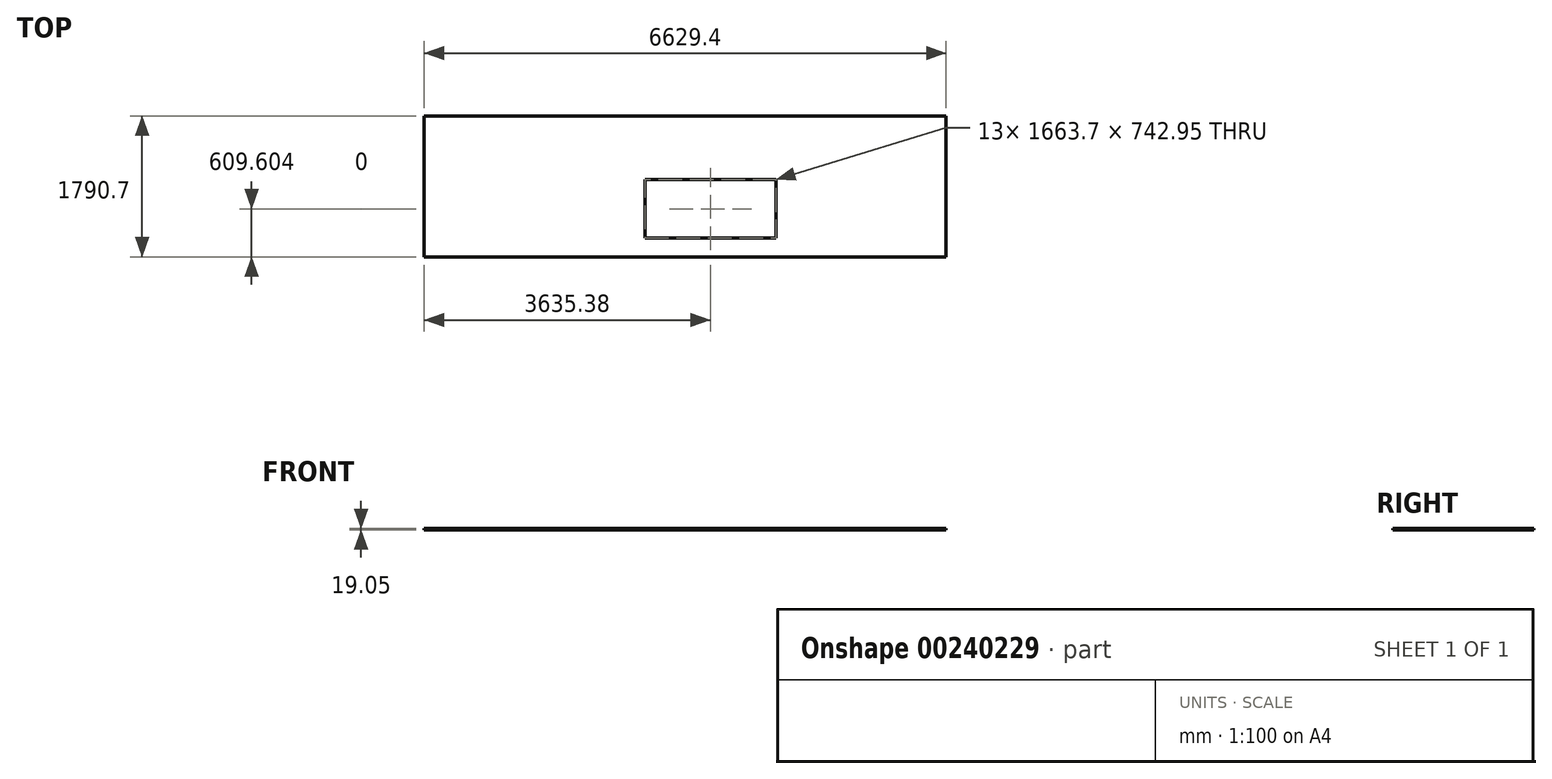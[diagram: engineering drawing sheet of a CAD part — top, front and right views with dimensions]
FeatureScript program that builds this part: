
annotation { "Feature Type Name" : "Feature", "Feature Type Description" : "" }
export const myFeature = defineFeature(function(context is Context, id is Id, definition is map)
    precondition{}
    {
        {
            var Q0;
            Q0=qCreatedBy(makeId("Top.planeOp"),FACE);
            var sketch = newSketch(context, id + "F0", { "sketchPlane" : qUnion([Q0])});
            skLineSegment(sketch, "E0.top", {"start": v(3079.82, 1055.16) * mm, "end": v(-3549.58, 1055.16) * mm});
            skLineSegment(sketch, "E0.left", {"start": v(3079.82, 1055.16) * mm, "end": v(3079.82, 1055.16) * mm});
            skLineSegment(sketch, "E1.top", {"start": v(-3549.58, -735.54) * mm, "end": v(3079.82, -735.54) * mm});
            skLineSegment(sketch, "E2.bottom", {"start": v(-3549.58, 1055.16) * mm, "end": v(3079.82, 1055.16) * mm});
            skLineSegment(sketch, "E2.left", {"start": v(-3549.58, 1055.16) * mm, "end": v(-3549.58, -735.54) * mm});
            skLineSegment(sketch, "E2.right", {"start": v(3079.82, 1055.16) * mm, "end": v(3079.82, -735.54) * mm});
            skLineSegment(sketch, "E3.bottom", {"start": v(-746.05, 245.54) * mm, "end": v(917.65, 245.54) * mm});
            skLineSegment(sketch, "E3.top", {"start": v(-746.05, -497.41) * mm, "end": v(917.65, -497.41) * mm});
            skLineSegment(sketch, "E3.left", {"start": v(-746.05, 245.54) * mm, "end": v(-746.05, -497.41) * mm});
            skLineSegment(sketch, "E3.right", {"start": v(917.65, 245.54) * mm, "end": v(917.65, -497.41) * mm});
            skSolve(sketch);
        }
        {
            var Q0;
            Q0=makeQuery(id+"F0.imprint","IMPRINT",FACE,{"disambiguationData":[TD([[makeQuery(id+"F0.imprint","IMPRINT",EDGE,{"derivedFrom":sQuery(id+"F0.wireOp",EDGE,"E1.top")}),1.0]])]});
            extrude(context, id + "F1", {"entities" : qUnion([Q0]), "depth" : 19.05 * mm});
        }
    });
